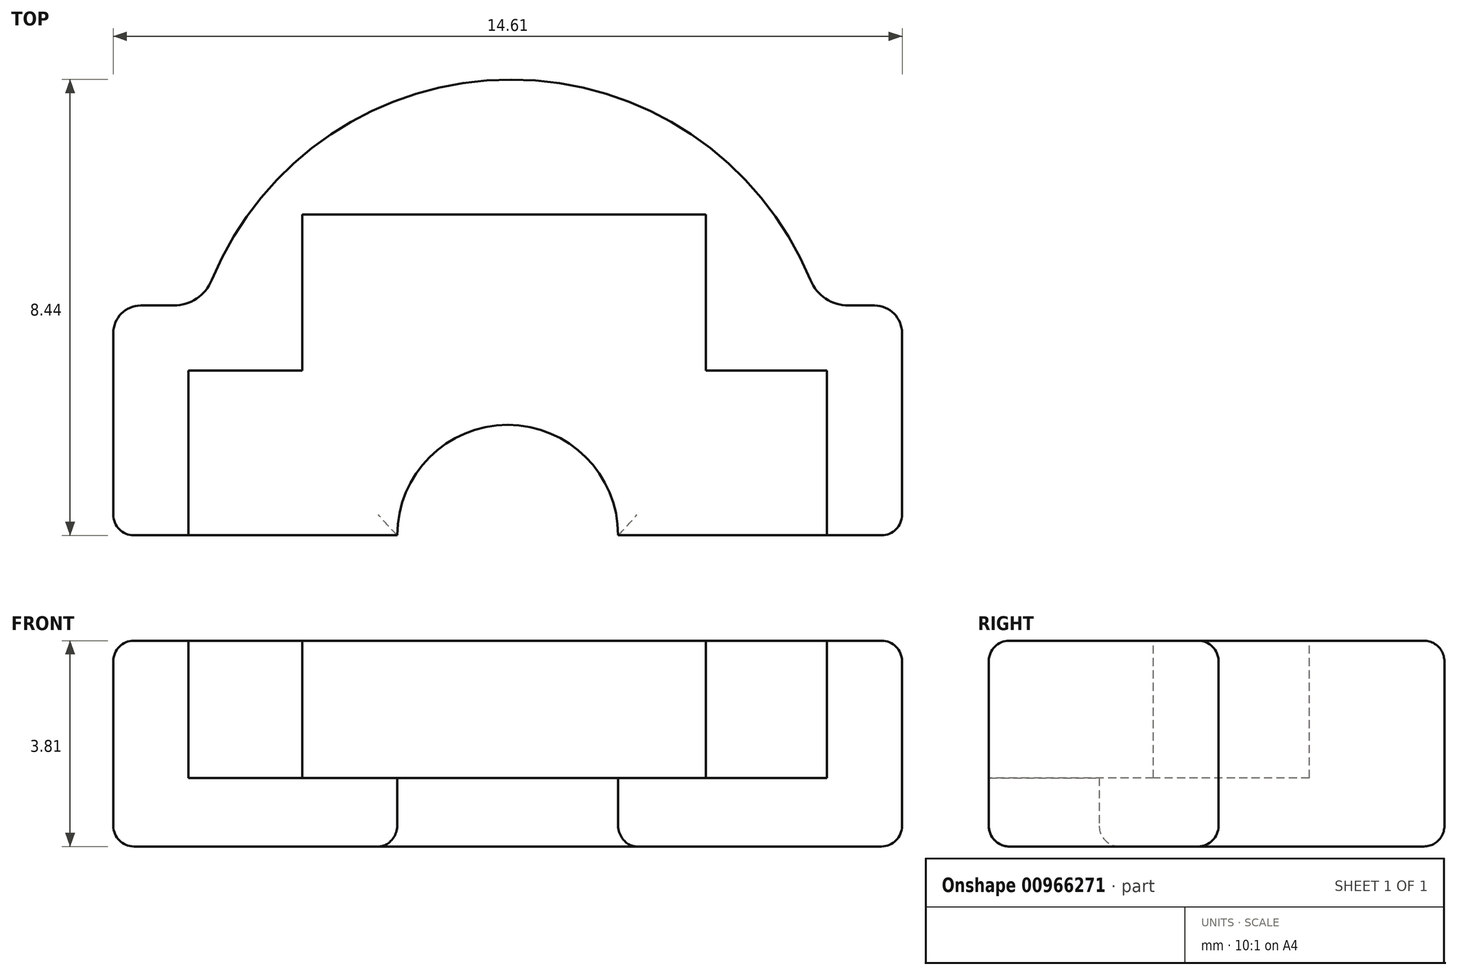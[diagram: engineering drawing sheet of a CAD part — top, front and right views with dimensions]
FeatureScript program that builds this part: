
annotation { "Feature Type Name" : "Feature", "Feature Type Description" : "" }
export const myFeature = defineFeature(function(context is Context, id is Id, definition is map)
    precondition{}
    {
        {
            var Q0;
            Q0=qCreatedBy(makeId("Top.planeOp"),FACE);
            var sketch = newSketch(context, id + "F0", { "sketchPlane" : qUnion([Q0])});
            skLineSegment(sketch, "E0.top", {"start": v(0, -8.5) * mm, "end": v(5.26, -8.5) * mm});
            skLineSegment(sketch, "E0.left", {"start": v(0, -4.25) * mm, "end": v(0, -8.5) * mm});
            skLineSegment(sketch, "E0.right", {"start": v(14.6, -4.25) * mm, "end": v(14.6, -8.5) * mm});
            skLineSegment(sketch, "E1", {"start": v(0, -4.25) * mm, "end": v(1.65, -4.25) * mm});
            skPoint(sketch, "E2.endSnap0", {"position": v(7.3, -4.25) * mm});
            skPoint(sketch, "E3.orphan", {"position": v(0, 0) * mm});
            skPoint(sketch, "E4.orphan", {"position": v(14.6, 0) * mm});
            skLineSegment(sketch, "E5.trimOffspring", {"start": v(13.08, -4.25) * mm, "end": v(14.6, -4.25) * mm});
            skArc(sketch, "E6", {"start": v(13.08, -4.25) * mm, "mid": v(7.37, -0.07) * mm, "end": v(1.65, -4.25) * mm});
            skArc(sketch, "E7", {"start": v(9.35, -8.5) * mm, "mid": v(7.3, -6.46) * mm, "end": v(5.26, -8.5) * mm});
            skLineSegment(sketch, "E8.trimOffspring", {"start": v(9.35, -8.5) * mm, "end": v(14.6, -8.5) * mm});
            skSolve(sketch);
        }
        {
            var Q0;
            Q0=makeQuery(id+"F0.imprint","IMPRINT",FACE,{"disambiguationData":[TD([[makeQuery(id+"F0.imprint","IMPRINT",EDGE,{"derivedFrom":sQuery(id+"F0.wireOp",EDGE,"E0.top")}),1.0]])]});
            extrude(context, id + "F1", {"entities" : qUnion([Q0]), "depth" : 3.8 * mm, "offsetDistance" : 25.4 * mm});
        }
        {
            var Q0;
            Q0=makeQuery(id+"F1.opExtrude","SWEPT_EDGE",EDGE,{"disambiguationData":[OSD([sQuery(id+"F0.wireOp",EDGE,"E5.trimOffspring"),sQuery(id+"F0.wireOp",EDGE,"E6")])]});
            var Q1;
            Q1=makeQuery(id+"F1.opExtrude","SWEPT_EDGE",EDGE,{"disambiguationData":[OSD([sQuery(id+"F0.wireOp",EDGE,"E1"),sQuery(id+"F0.wireOp",EDGE,"E6")])]});
            fillet(context, id + "F2", {"entities" : qUnion([Q0, Q1]), "radius" : 0.76 * mm, "tangentPropagation" : true, "allowEdgeOverflow" : false});
        }
        {
            var Q0;
            Q0=makeQuery(id+"F1.opExtrude","SWEPT_EDGE",EDGE,{"disambiguationData":[OSD([sQuery(id+"F0.wireOp",EDGE,"E0.left"),sQuery(id+"F0.wireOp",EDGE,"E1")])]});
            var Q1;
            Q1=makeQuery(id+"F1.opExtrude","SWEPT_EDGE",EDGE,{"disambiguationData":[OSD([sQuery(id+"F0.wireOp",EDGE,"E0.right"),sQuery(id+"F0.wireOp",EDGE,"E5.trimOffspring")])]});
            fillet(context, id + "F3", {"entities" : qUnion([Q0, Q1]), "radius" : 0.5 * mm, "tangentPropagation" : true, "allowEdgeOverflow" : false});
        }
        {
            var Q0;
            Q0=makeQuery(id+"F1.opExtrude","CAP_FACE",FACE,{"disambiguationData":[OSD([sQuery(id+"F0.wireOp",EDGE,"E0.top"),sQuery(id+"F0.wireOp",EDGE,"E0.left"),sQuery(id+"F0.wireOp",EDGE,"E0.right"),sQuery(id+"F0.wireOp",EDGE,"E1"),sQuery(id+"F0.wireOp",EDGE,"E5.trimOffspring"),sQuery(id+"F0.wireOp",EDGE,"E6"),sQuery(id+"F0.wireOp",EDGE,"E7"),sQuery(id+"F0.wireOp",EDGE,"E8.trimOffspring")])],"isStart":true});
            fillet(context, id + "F4", {"entities" : qUnion([Q0]), "radius" : 0.38 * mm, "tangentPropagation" : true, "allowEdgeOverflow" : false});
        }
        {
            var Q0;
            Q0=makeQuery(id+"F1.opExtrude","CAP_FACE",FACE,{"disambiguationData":[OSD([sQuery(id+"F0.wireOp",EDGE,"E0.top"),sQuery(id+"F0.wireOp",EDGE,"E0.left"),sQuery(id+"F0.wireOp",EDGE,"E0.right"),sQuery(id+"F0.wireOp",EDGE,"E1"),sQuery(id+"F0.wireOp",EDGE,"E5.trimOffspring"),sQuery(id+"F0.wireOp",EDGE,"E6"),sQuery(id+"F0.wireOp",EDGE,"E7"),sQuery(id+"F0.wireOp",EDGE,"E8.trimOffspring")])],"isStart":false});
            var Q1;
            Q1=makeQuery(id+"F1.opExtrude","SWEPT_EDGE",EDGE,{"disambiguationData":[OSD([sQuery(id+"F0.wireOp",EDGE,"E0.top"),sQuery(id+"F0.wireOp",EDGE,"E0.left")])]});
            var Q2;
            Q2=makeQuery(id+"F1.opExtrude","SWEPT_EDGE",EDGE,{"disambiguationData":[OSD([sQuery(id+"F0.wireOp",EDGE,"E0.right"),sQuery(id+"F0.wireOp",EDGE,"E8.trimOffspring")])]});
            fillet(context, id + "F5", {"entities" : qUnion([Q0, Q1, Q2]), "radius" : 0.38 * mm, "tangentPropagation" : true, "allowEdgeOverflow" : false});
        }
        {
            var Q0;
            Q0=makeQuery(id+"F1.opExtrude","CAP_FACE",FACE,{"disambiguationData":[OSD([sQuery(id+"F0.wireOp",EDGE,"E0.top"),sQuery(id+"F0.wireOp",EDGE,"E0.left"),sQuery(id+"F0.wireOp",EDGE,"E0.right"),sQuery(id+"F0.wireOp",EDGE,"E1"),sQuery(id+"F0.wireOp",EDGE,"E5.trimOffspring"),sQuery(id+"F0.wireOp",EDGE,"E6"),sQuery(id+"F0.wireOp",EDGE,"E7"),sQuery(id+"F0.wireOp",EDGE,"E8.trimOffspring")])],"isStart":false});
            var sketch = newSketch(context, id + "F6", { "sketchPlane" : qUnion([Q0])});
            skLineSegment(sketch, "E9", {"start": v(1.4, -8.8) * mm, "end": v(1.4, -5.46) * mm});
            skLineSegment(sketch, "E10", {"start": v(1.4, -5.46) * mm, "end": v(3.5, -5.46) * mm});
            skLineSegment(sketch, "E11", {"start": v(3.5, -5.46) * mm, "end": v(3.5, -2.57) * mm});
            skLineSegment(sketch, "E12", {"start": v(3.5, -2.57) * mm, "end": v(10.97, -2.57) * mm});
            skLineSegment(sketch, "E13", {"start": v(10.97, -2.57) * mm, "end": v(10.97, -5.46) * mm});
            skLineSegment(sketch, "E14", {"start": v(10.97, -5.46) * mm, "end": v(13.22, -5.46) * mm});
            skLineSegment(sketch, "E15", {"start": v(13.22, -5.46) * mm, "end": v(13.22, -9.26) * mm});
            skLineSegment(sketch, "E16", {"start": v(13.22, -9.26) * mm, "end": v(1.4, -9.26) * mm});
            skLineSegment(sketch, "E17", {"start": v(1.4, -9.26) * mm, "end": v(1.4, -8.8) * mm});
            skSolve(sketch);
        }
        {
            var Q0;
            Q0 = qSketchRegion(id + "F6", true);
            extrude(context, id + "F7", {"entities" : qUnion([Q0]), "operationType" : NewBodyOperationType.REMOVE, "oppositeDirection" : true, "depth" : 2.54 * mm, "offsetDistance" : 25.4 * mm});
        }
    });
